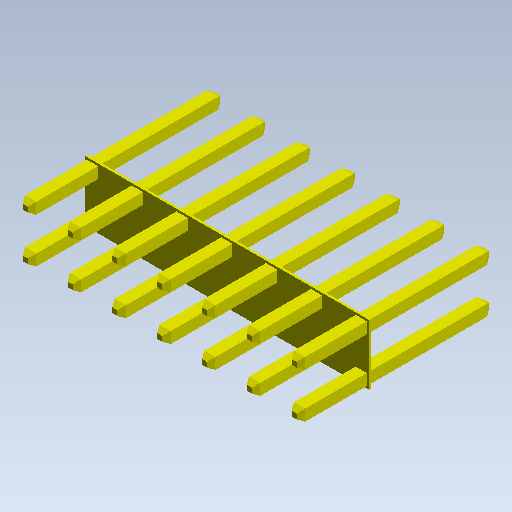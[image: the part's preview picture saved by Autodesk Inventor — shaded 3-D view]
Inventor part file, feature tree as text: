
AUTODESK INVENTOR PART (.ipt)
format: ipt  version: 2021 (Build 250183000, 183)  size: 379,392 bytes
history: native  units: mm (DEFAULTED — no unit token found)
features: other x14, extrude x10, sketch x10
ambient origin geometry x8: Origin, YZ Plane, XZ Plane, XY Plane, X Axis, Y Axis, Z Axis, Center Point
bodies: Solid1 (feature_tree)
feature tree (34):
  extrude  "Extrusion1"  Depth=16.129mm TaperAngle=0.0deg
  extrude  "Extrusion2"  Depth=10.16mm TaperAngle=0.0deg
  extrude  "Extrusion3"  Depth=35.56mm TaperAngle=0.0deg
  extrude  "Extrusion4"  Depth=35.56mm TaperAngle=0.0deg
  extrude  "Extrusion5"  Depth=10.16mm TaperAngle=0.0deg
  extrude  "Extrusion6"  [1 undecoded]
  extrude  "Extrusion7"  [1 undecoded]
  extrude  "Extrusion8"  [1 undecoded]
  extrude  "Extrusion9"  [1 undecoded]
  extrude  "Extrusion10"  [1 undecoded]
  other  "pin_XY"
  other  "pin_YZ"
  other  "pin_ZX"
  other  "pin_X"
  other  "pin_Y"
  other  "pin_Z"
  other  "pin_Center"
  other  "zst_prj_pin_XY"
  other  "zst_prj_pin_YZ"
  other  "zst_prj_pin_ZX"
  other  "zst_prj_pin_X"
  other  "zst_prj_pin_Y"
  other  "zst_prj_pin_Z"
  other  "zst_prj_pin_Center"
  sketch  "Sketch_1"  dims[d0=3.175mm d1=0.0mm d2=16.129mm d3=0.0mm]
  sketch  "Sketch_26"
  sketch  "Sketch_9"  dims[d4=10.16mm d5=0.0mm d6=10.16mm d7=0.0mm]
  sketch  "Sketch_12"  dims[d8=35.56mm d9=0.0mm d10=35.56mm d11=0.0mm]
  sketch  "Sketch_14"  dims[d12=35.56mm d13=0.0mm d14=35.56mm d15=0.0mm]
  sketch  "Sketch_16"  dims[d16=10.16mm d17=0.0mm d18=10.16mm d19=0.0mm]
  sketch  "Sketch_40"
  sketch  "Sketch_44"
  sketch  "Sketch_45"
  sketch  "Sketch_46"
note: 5 required parameter values undecoded (feature->parameter linkage not recoverable at this tier; creation-order binding heuristic only, values carry confidence <= 0.55)
